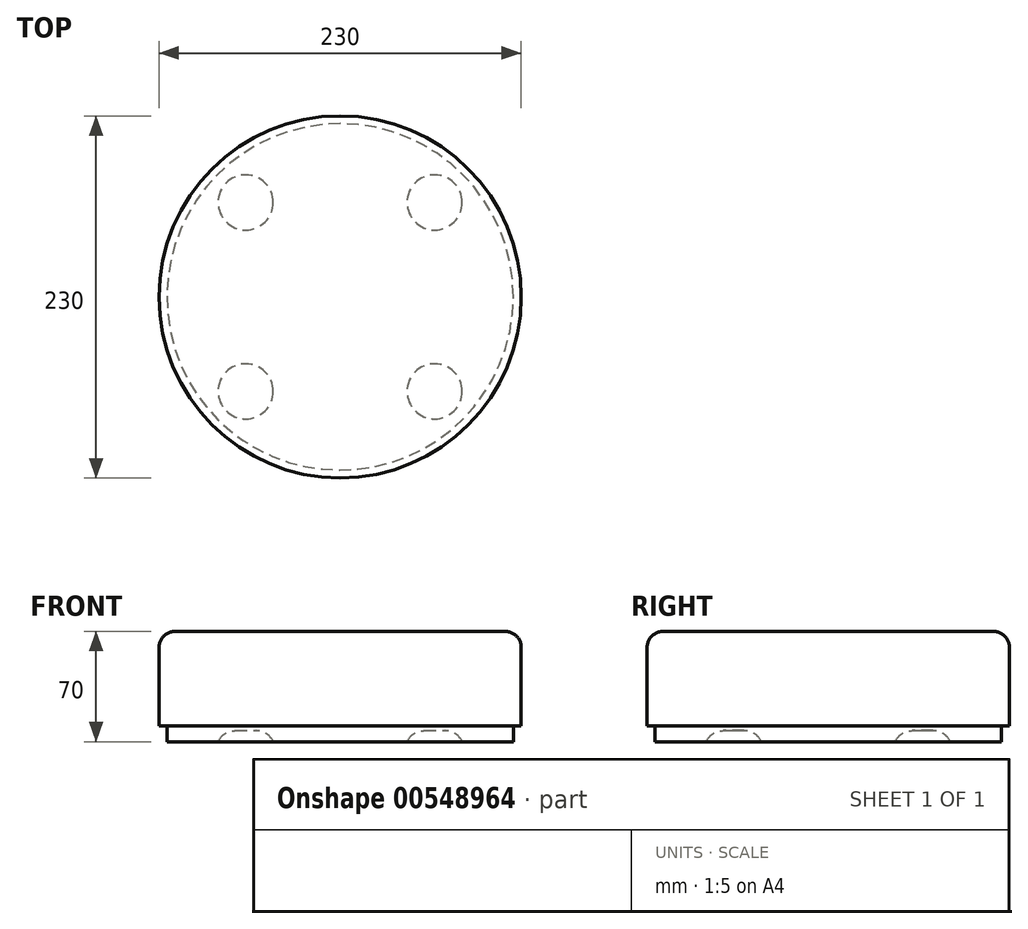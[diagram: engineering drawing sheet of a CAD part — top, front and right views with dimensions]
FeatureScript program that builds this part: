
annotation { "Feature Type Name" : "Feature", "Feature Type Description" : "" }
export const myFeature = defineFeature(function(context is Context, id is Id, definition is map)
    precondition{}
    {
        {
            var Q0;
            Q0=qCreatedBy(makeId("Top.planeOp"),FACE);
            var sketch = newSketch(context, id + "F0", { "sketchPlane" : qUnion([Q0])});
            skCircle(sketch, "E0", {"center": v(0, 0) * mm, "radius": 115 * mm});
            skSolve(sketch);
        }
        {
            var Q0;
            Q0 = qSketchRegion(id + "F0", true);
            extrude(context, id + "F1", {"entities" : qUnion([Q0]), "depth" : 70 * mm, "offsetDistance" : 25 * mm});
        }
        {
            var Q0;
            Q0=makeQuery(id+"F1.opExtrude","CAP_FACE",FACE,{"disambiguationData":[OSD([sQuery(id+"F0.wireOp",EDGE,"E0")])],"isStart":true});
            var sketch = newSketch(context, id + "F2", { "sketchPlane" : qUnion([Q0])});
            skCircle(sketch, "E1", {"center": v(-60, 60) * mm, "radius": 17.5 * mm});
            skCircle(sketch, "E2.1.0", {"center": v(-60, -60) * mm, "radius": 17.5 * mm});
            skCircle(sketch, "E2.2.0", {"center": v(60, -60) * mm, "radius": 17.5 * mm});
            skCircle(sketch, "E2.3.0", {"center": v(60, 60) * mm, "radius": 17.5 * mm});
            skPoint(sketch, "E2.center", {"position": v(0, 0) * mm});
            skSolve(sketch);
        }
        {
            var Q0;
            Q0 = qSketchRegion(id + "F2", true);
            extrude(context, id + "F3", {"entities" : qUnion([Q0]), "operationType" : NewBodyOperationType.REMOVE, "oppositeDirection" : true, "depth" : 7 * mm, "offsetDistance" : 25 * mm});
        }
        {
            var Q0;
            Q0=makeQuery(id+"F3.boolean.opBoolean","COPY",EDGE,{"derivedFrom":makeQuery(id+"F3.opExtrude","CAP_EDGE",EDGE,{"disambiguationData":[OSD([sQuery(id+"F2.wireOp",EDGE,"E1")])],"isStart":false})});
            var Q1;
            Q1=makeQuery(id+"F3.boolean.opBoolean","COPY",EDGE,{"derivedFrom":makeQuery(id+"F3.opExtrude","CAP_EDGE",EDGE,{"disambiguationData":[OSD([sQuery(id+"F2.wireOp",EDGE,"E2.1.0")])],"isStart":false})});
            var Q2;
            Q2=makeQuery(id+"F3.boolean.opBoolean","COPY",EDGE,{"derivedFrom":makeQuery(id+"F3.opExtrude","CAP_EDGE",EDGE,{"disambiguationData":[OSD([sQuery(id+"F2.wireOp",EDGE,"E2.2.0")])],"isStart":false})});
            var Q3;
            Q3=makeQuery(id+"F3.boolean.opBoolean","COPY",EDGE,{"derivedFrom":makeQuery(id+"F3.opExtrude","CAP_EDGE",EDGE,{"disambiguationData":[OSD([sQuery(id+"F2.wireOp",EDGE,"E2.3.0")])],"isStart":false})});
            fillet(context, id + "F4", {"entities" : qUnion([Q0, Q1, Q2, Q3]), "radius" : 12 * mm, "tangentPropagation" : true, "allowEdgeOverflow" : false});
        }
        {
            var Q0;
            Q0=makeQuery(id+"F1.opExtrude","CAP_EDGE",EDGE,{"disambiguationData":[OSD([sQuery(id+"F0.wireOp",EDGE,"E0")])],"isStart":false});
            fillet(context, id + "F5", {"entities" : qUnion([Q0]), "radius" : 10 * mm, "tangentPropagation" : true, "allowEdgeOverflow" : false});
        }
        {
            var Q0;
            Q0=makeQuery(id+"F1.opExtrude","CAP_FACE",FACE,{"disambiguationData":[OSD([sQuery(id+"F0.wireOp",EDGE,"E0")])],"isStart":true});
            var sketch = newSketch(context, id + "F6", { "sketchPlane" : qUnion([Q0])});
            skCircle(sketch, "E3", {"center": v(0, 0) * mm, "radius": 110 * mm});
            skCircle(sketch, "E4", {"center": v(0, 0) * mm, "radius": 115 * mm});
            skSolve(sketch);
        }
        {
            var Q0;
            Q0 = qSketchRegion(id + "F6", true);
            extrude(context, id + "F7", {"entities" : qUnion([Q0]), "operationType" : NewBodyOperationType.REMOVE, "oppositeDirection" : true, "depth" : 10 * mm, "offsetDistance" : 25 * mm});
        }
    });
